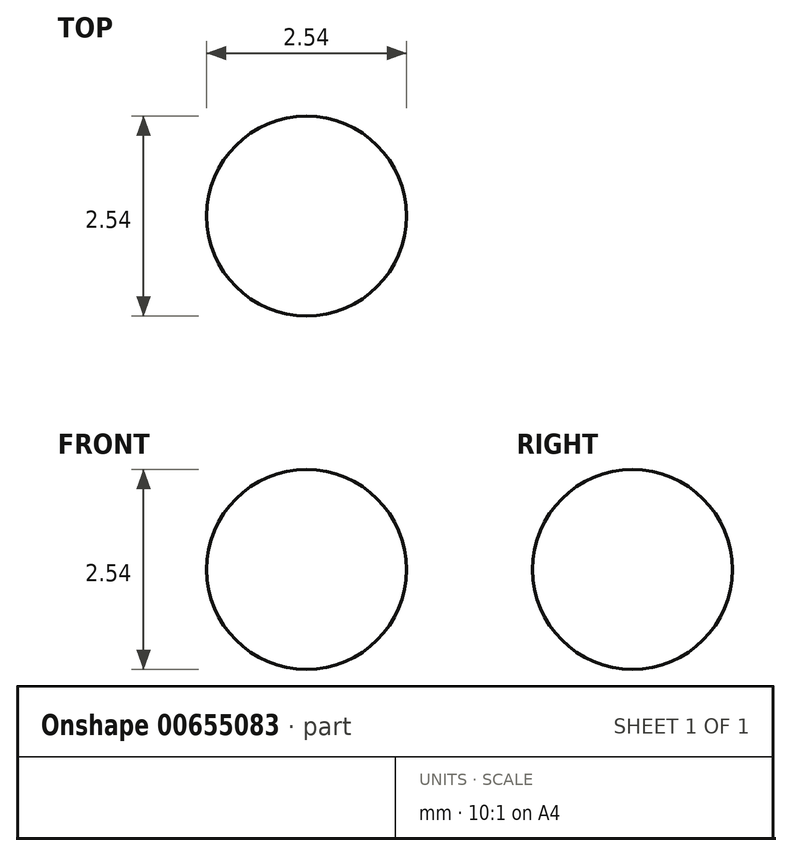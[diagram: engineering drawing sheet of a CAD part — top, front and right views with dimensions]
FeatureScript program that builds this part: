
annotation { "Feature Type Name" : "Feature", "Feature Type Description" : "" }
export const myFeature = defineFeature(function(context is Context, id is Id, definition is map)
    precondition{}
    {
        {
            var Q0;
            Q0=qCreatedBy(makeId("Front.planeOp"),FACE);
            var sketch = newSketch(context, id + "F0", { "sketchPlane" : qUnion([Q0])});
            skCircle(sketch, "E0", {"center": v(0, 0) * mm, "radius": 1.27 * mm});
            skLineSegment(sketch, "E1", {"start": v(0, 3.58) * mm, "end": v(0, -3.98) * mm});
            skSolve(sketch);
        }
        {
            var Q0;
            {var subQ0=sQuery(id+"F0.wireOp",EDGE,"E1");var subQ1=sQuery(id+"F0.wireOp",EDGE,"E0");var subQ2=makeQuery(id+"F0.imprint","INTERSECT",VERTEX,{"disambiguationData":[OD(0.0)],"derivedFrom":[subQ1,subQ0]});Q0=makeQuery(id+"F0.imprint","IMPRINT",FACE,{"disambiguationData":[TD([[makeQuery(id+"F0.imprint","IMPRINT",EDGE,{"disambiguationData":[TD([[subQ2,1.0]])],"derivedFrom":subQ1}),1.0]])]});}
            var Q1;
            Q1=sQuery(id+"F0.wireOp",EDGE,"E1");
            revolve(context, id + "F1", {"entities" : qUnion([Q0]), "axis" : qUnion([Q1]), "revolveType" : RevolveType.FULL});
        }
    });
